AUTODESK INVENTOR PART (.ipt)
format: ipt  version: 2019 (Build 230136000, 136)  size: 96,768 bytes
history: native  units: in
note: dims shown in document units (in); Inventor stores cm internally (conversion verified against a paired STEP export)
features: sketch x1
ambient origin geometry x8: Origin, YZ Plane, XZ Plane, XY Plane, X Axis, Y Axis, Z Axis, Center Point
feature tree (1):
  sketch  "Sketch1"  dims[d4=0.0394in d5=0.0394in d6=0.0394in d7=0.0394in d8=0.0394in d9=0.0394in d10=0.0394in d11=0.0394in d12=0.0394in d13=0.0394in d14=0.0197in d15=0.0197in d16=0.7087in]
